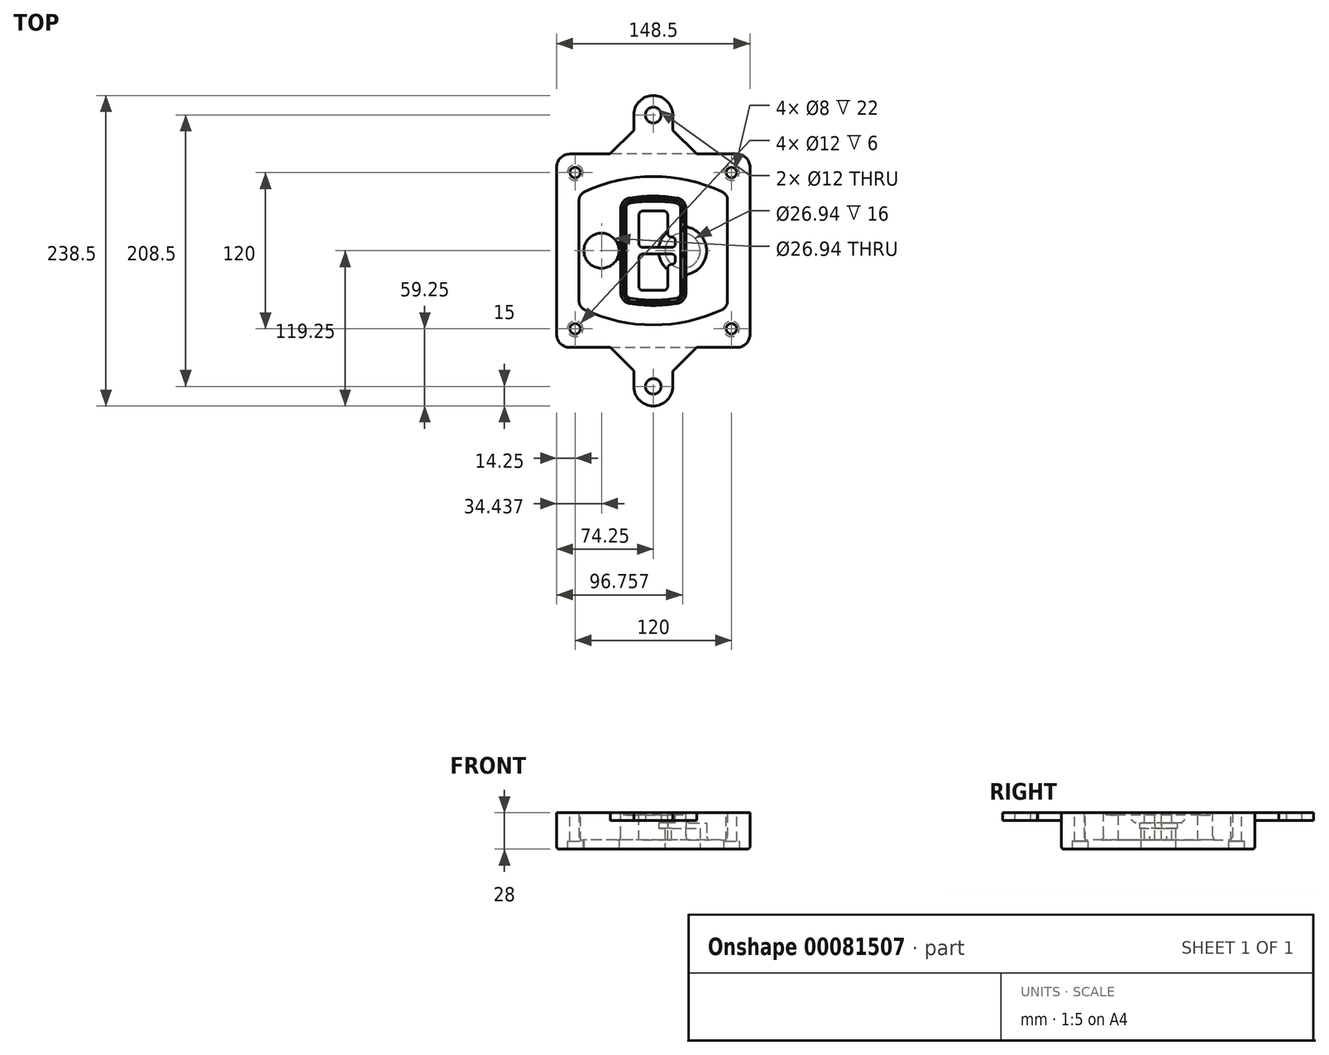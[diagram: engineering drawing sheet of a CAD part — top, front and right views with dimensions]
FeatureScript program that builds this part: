
annotation { "Feature Type Name" : "Feature", "Feature Type Description" : "" }
export const myFeature = defineFeature(function(context is Context, id is Id, definition is map)
    precondition{}
    {
        {
            var Q0;
            Q0=qCreatedBy(makeId("Top.planeOp"),FACE);
            var sketch = newSketch(context, id + "F0", { "sketchPlane" : qUnion([Q0])});
            skPoint(sketch, "E0.rect.middle", {"position": v(0, 0) * mm});
            skLineSegment(sketch, "E1.bottom", {"start": v(-64.25, -74.25) * mm, "end": v(64.25, -74.25) * mm});
            skLineSegment(sketch, "E1.top", {"start": v(-64.25, 74.25) * mm, "end": v(64.25, 74.25) * mm});
            skLineSegment(sketch, "E1.left", {"start": v(-74.25, -64.25) * mm, "end": v(-74.25, 64.25) * mm});
            skLineSegment(sketch, "E1.right", {"start": v(74.25, -64.25) * mm, "end": v(74.25, 64.25) * mm});
            skLineSegment(sketch, "E2", {"start": v(-74.25, 74.25) * mm, "end": v(74.25, -74.25) * mm, "construction": true});
            skLineSegment(sketch, "E3", {"start": v(74.25, 74.25) * mm, "end": v(-74.25, -74.25) * mm, "construction": true});
            skCircle(sketch, "E4", {"center": v(-60, 60) * mm, "radius": 4 * mm});
            skCircle(sketch, "E5", {"center": v(60, 60) * mm, "radius": 4 * mm});
            skCircle(sketch, "E6", {"center": v(60, -60) * mm, "radius": 4 * mm});
            skCircle(sketch, "E7", {"center": v(-60, -60) * mm, "radius": 4 * mm});
            skLineSegment(sketch, "E8", {"start": v(-60, 60) * mm, "end": v(60, 60) * mm, "construction": true});
            skLineSegment(sketch, "E9", {"start": v(60, 60) * mm, "end": v(60, -60) * mm, "construction": true});
            skLineSegment(sketch, "E10", {"start": v(60, -60) * mm, "end": v(-60, -60) * mm, "construction": true});
            skLineSegment(sketch, "E11", {"start": v(-60, -60) * mm, "end": v(-60, 60) * mm, "construction": true});
            skLineSegment(sketch, "E12", {"start": v(-60, 38.83) * mm, "end": v(-60, -38.83) * mm});
            skLineSegment(sketch, "E13", {"start": v(60, 38.83) * mm, "end": v(60, -38.83) * mm});
            skArc(sketch, "E14", {"start": v(54.26, 47.88) * mm, "mid": v(0, 60) * mm, "end": v(-54.26, 47.88) * mm});
            skArc(sketch, "E15", {"start": v(-54.26, -47.88) * mm, "mid": v(0, -60) * mm, "end": v(54.26, -47.88) * mm});
            skLineSegment(sketch, "E16", {"start": v(-60, 0) * mm, "end": v(60, 0) * mm, "construction": true});
            skPoint(sketch, "E17.visualSharp", {"position": v(-60, -45) * mm});
            skArc(sketch, "E17.filletArc", {"start": v(-60, -38.83) * mm, "mid": v(-58.44, -44.2) * mm, "end": v(-54.26, -47.88) * mm});
            skPoint(sketch, "E18.visualSharp", {"position": v(-60, 45) * mm});
            skArc(sketch, "E18.filletArc", {"start": v(-54.26, 47.88) * mm, "mid": v(-58.44, 44.2) * mm, "end": v(-60, 38.83) * mm});
            skPoint(sketch, "E19.visualSharp", {"position": v(60, 45) * mm});
            skArc(sketch, "E19.filletArc", {"start": v(60, 38.83) * mm, "mid": v(58.44, 44.2) * mm, "end": v(54.26, 47.88) * mm});
            skPoint(sketch, "E20.visualSharp", {"position": v(60, -45) * mm});
            skArc(sketch, "E20.filletArc", {"start": v(54.26, -47.88) * mm, "mid": v(58.44, -44.2) * mm, "end": v(60, -38.83) * mm});
            skPoint(sketch, "E21.visualSharp", {"position": v(-74.25, 74.25) * mm});
            skArc(sketch, "E21.filletArc", {"start": v(-64.25, 74.25) * mm, "mid": v(-71.32, 71.32) * mm, "end": v(-74.25, 64.25) * mm});
            skPoint(sketch, "E22.visualSharp", {"position": v(74.25, 74.25) * mm});
            skArc(sketch, "E22.filletArc", {"start": v(74.25, 64.25) * mm, "mid": v(71.32, 71.32) * mm, "end": v(64.25, 74.25) * mm});
            skPoint(sketch, "E23.visualSharp", {"position": v(74.25, -74.25) * mm});
            skArc(sketch, "E23.filletArc", {"start": v(64.25, -74.25) * mm, "mid": v(71.32, -71.32) * mm, "end": v(74.25, -64.25) * mm});
            skPoint(sketch, "E24.visualSharp", {"position": v(-74.25, -74.25) * mm});
            skArc(sketch, "E24.filletArc", {"start": v(-74.25, -64.25) * mm, "mid": v(-71.32, -71.32) * mm, "end": v(-64.25, -74.25) * mm});
            skArc(sketch, "E25.0", {"start": v(57, 38.83) * mm, "mid": v(55.9, 42.58) * mm, "end": v(52.98, 45.17) * mm});
            skLineSegment(sketch, "E25.1", {"start": v(57, 38.83) * mm, "end": v(57, -38.83) * mm});
            skArc(sketch, "E25.2", {"start": v(52.98, -45.17) * mm, "mid": v(55.9, -42.58) * mm, "end": v(57, -38.83) * mm});
            skArc(sketch, "E25.3", {"start": v(-52.98, -45.17) * mm, "mid": v(0, -57) * mm, "end": v(52.98, -45.17) * mm});
            skArc(sketch, "E25.4", {"start": v(-57, -38.83) * mm, "mid": v(-55.9, -42.58) * mm, "end": v(-52.98, -45.17) * mm});
            skArc(sketch, "E25.5", {"start": v(52.98, 45.17) * mm, "mid": v(0, 57) * mm, "end": v(-52.98, 45.17) * mm});
            skLineSegment(sketch, "E25.6", {"start": v(-57, 38.83) * mm, "end": v(-57, -38.83) * mm});
            skArc(sketch, "E25.7", {"start": v(-52.98, 45.17) * mm, "mid": v(-55.9, 42.58) * mm, "end": v(-57, 38.83) * mm});
            skArc(sketch, "E26.0", {"start": v(-55.96, 51.5) * mm, "mid": v(-61.82, 46.33) * mm, "end": v(-64, 38.83) * mm});
            skArc(sketch, "E26.1", {"start": v(55.96, 51.5) * mm, "mid": v(0, 64) * mm, "end": v(-55.96, 51.5) * mm});
            skArc(sketch, "E26.2", {"start": v(64, 38.83) * mm, "mid": v(61.82, 46.33) * mm, "end": v(55.96, 51.5) * mm});
            skLineSegment(sketch, "E26.3", {"start": v(64, 38.83) * mm, "end": v(64, -38.83) * mm});
            skArc(sketch, "E26.4", {"start": v(55.96, -51.5) * mm, "mid": v(61.82, -46.33) * mm, "end": v(64, -38.83) * mm});
            skLineSegment(sketch, "E26.5", {"start": v(-64, 38.83) * mm, "end": v(-64, -38.83) * mm});
            skArc(sketch, "E26.6", {"start": v(-55.96, -51.5) * mm, "mid": v(0, -64) * mm, "end": v(55.96, -51.5) * mm});
            skArc(sketch, "E26.7", {"start": v(-64, -38.83) * mm, "mid": v(-61.82, -46.33) * mm, "end": v(-55.96, -51.5) * mm});
            skSolve(sketch);
        }
        {
            var Q0;
            Q0=makeQuery(id+"F0.imprint","IMPRINT",FACE,{"disambiguationData":[TD([[makeQuery(id+"F0.imprint","IMPRINT",EDGE,{"derivedFrom":sQuery(id+"F0.wireOp",EDGE,"E1.bottom")}),1.0]])]});
            var Q1;
            Q1=makeQuery(id+"F0.imprint","IMPRINT",FACE,{"disambiguationData":[TD([[makeQuery(id+"F0.imprint","IMPRINT",EDGE,{"derivedFrom":sQuery(id+"F0.wireOp",EDGE,"E12")}),1.0]])]});
            var Q2;
            Q2=makeQuery(id+"F0.imprint","IMPRINT",FACE,{"disambiguationData":[TD([[makeQuery(id+"F0.imprint","IMPRINT",EDGE,{"derivedFrom":sQuery(id+"F0.wireOp",EDGE,"E25.0")}),1.0]])]});
            var Q3;
            Q3=makeQuery(id+"F0.imprint","IMPRINT",FACE,{"disambiguationData":[TD([[makeQuery(id+"F0.imprint","IMPRINT",EDGE,{"derivedFrom":sQuery(id+"F0.wireOp",EDGE,"E12")}),-1.0]])]});
            extrude(context, id + "F1", {"entities" : qUnion([Q0, Q1, Q2, Q3]), "oppositeDirection" : true, "depth" : 25 * mm});
        }
        {
            var Q0;
            Q0=makeQuery(id+"F0.imprint","IMPRINT",FACE,{"disambiguationData":[TD([[makeQuery(id+"F0.imprint","IMPRINT",EDGE,{"derivedFrom":sQuery(id+"F0.wireOp",EDGE,"E12")}),1.0]])]});
            extrude(context, id + "F2", {"entities" : qUnion([Q0]), "operationType" : NewBodyOperationType.ADD, "depth" : 3 * mm});
        }
        {
            var Q0;
            Q0=makeQuery(id+"F0.imprint","IMPRINT",FACE,{"disambiguationData":[TD([[makeQuery(id+"F0.imprint","IMPRINT",EDGE,{"derivedFrom":sQuery(id+"F0.wireOp",EDGE,"E25.0")}),1.0]])]});
            extrude(context, id + "F3", {"entities" : qUnion([Q0]), "operationType" : NewBodyOperationType.REMOVE, "oppositeDirection" : true, "depth" : 18 * mm});
        }
        {
            var Q0;
            Q0=makeQuery(id+"F2.opExtrude","CAP_FACE",FACE,{"disambiguationData":[OSD([sQuery(id+"F0.wireOp",EDGE,"E12"),sQuery(id+"F0.wireOp",EDGE,"E13"),sQuery(id+"F0.wireOp",EDGE,"E14"),sQuery(id+"F0.wireOp",EDGE,"E15"),sQuery(id+"F0.wireOp",EDGE,"E17.filletArc"),sQuery(id+"F0.wireOp",EDGE,"E18.filletArc"),sQuery(id+"F0.wireOp",EDGE,"E19.filletArc"),sQuery(id+"F0.wireOp",EDGE,"E20.filletArc"),sQuery(id+"F0.wireOp",EDGE,"E25.0"),sQuery(id+"F0.wireOp",EDGE,"E25.1"),sQuery(id+"F0.wireOp",EDGE,"E25.2"),sQuery(id+"F0.wireOp",EDGE,"E25.3"),sQuery(id+"F0.wireOp",EDGE,"E25.4"),sQuery(id+"F0.wireOp",EDGE,"E25.5"),sQuery(id+"F0.wireOp",EDGE,"E25.6"),sQuery(id+"F0.wireOp",EDGE,"E25.7")])],"isStart":false});
            var sketch = newSketch(context, id + "F4", { "sketchPlane" : qUnion([Q0])});
            skArc(sketch, "E27.0", {"start": v(-18.34, -40.45) * mm, "mid": v(0, -42) * mm, "end": v(18.34, -40.45) * mm});
            skArc(sketch, "E28.0", {"start": v(18.34, 40.45) * mm, "mid": v(0, 42) * mm, "end": v(-18.34, 40.45) * mm});
            skLineSegment(sketch, "E29", {"start": v(-25, 32.57) * mm, "end": v(-25, -32.57) * mm});
            skLineSegment(sketch, "E30", {"start": v(25, 32.57) * mm, "end": v(25, -32.57) * mm});
            skLineSegment(sketch, "E31", {"start": v(-25, 39.1) * mm, "end": v(25, 39.1) * mm, "construction": true});
            skLineSegment(sketch, "E32", {"start": v(-25, -39.1) * mm, "end": v(25, -39.1) * mm, "construction": true});
            skPoint(sketch, "E33.visualSharp", {"position": v(-25, 39.1) * mm});
            skArc(sketch, "E33.filletArc", {"start": v(-18.34, 40.45) * mm, "mid": v(-23.11, 37.73) * mm, "end": v(-25, 32.57) * mm});
            skPoint(sketch, "E34.visualSharp", {"position": v(25, 39.1) * mm});
            skArc(sketch, "E34.filletArc", {"start": v(25, 32.57) * mm, "mid": v(23.11, 37.73) * mm, "end": v(18.34, 40.45) * mm});
            skPoint(sketch, "E35.visualSharp", {"position": v(25, -39.1) * mm});
            skArc(sketch, "E35.filletArc", {"start": v(18.34, -40.45) * mm, "mid": v(23.11, -37.73) * mm, "end": v(25, -32.57) * mm});
            skPoint(sketch, "E36.visualSharp", {"position": v(-25, -39.1) * mm});
            skArc(sketch, "E36.filletArc", {"start": v(-25, -32.57) * mm, "mid": v(-23.11, -37.73) * mm, "end": v(-18.34, -40.45) * mm});
            skArc(sketch, "E37.0", {"start": v(52.98, 45.17) * mm, "mid": v(0, 57) * mm, "end": v(-52.98, 45.17) * mm});
            skArc(sketch, "E37.1", {"start": v(-52.98, 45.17) * mm, "mid": v(-55.9, 42.58) * mm, "end": v(-57, 38.83) * mm});
            skLineSegment(sketch, "E37.2", {"start": v(-57, 38.83) * mm, "end": v(-57, -38.83) * mm});
            skArc(sketch, "E37.3", {"start": v(-57, -38.83) * mm, "mid": v(-55.9, -42.58) * mm, "end": v(-52.98, -45.17) * mm});
            skArc(sketch, "E37.4", {"start": v(-52.98, -45.17) * mm, "mid": v(0, -57) * mm, "end": v(52.98, -45.17) * mm});
            skArc(sketch, "E37.5", {"start": v(52.98, -45.17) * mm, "mid": v(55.9, -42.58) * mm, "end": v(57, -38.83) * mm});
            skLineSegment(sketch, "E37.6", {"start": v(57, 38.83) * mm, "end": v(57, -38.83) * mm});
            skArc(sketch, "E37.7", {"start": v(57, 38.83) * mm, "mid": v(55.9, 42.58) * mm, "end": v(52.98, 45.17) * mm});
            skLineSegment(sketch, "E38.0", {"start": v(23, 32.57) * mm, "end": v(23, -32.57) * mm});
            skArc(sketch, "E38.1", {"start": v(18, -38.48) * mm, "mid": v(21.58, -36.44) * mm, "end": v(23, -32.57) * mm});
            skArc(sketch, "E38.2", {"start": v(-18, -38.48) * mm, "mid": v(0, -40) * mm, "end": v(18, -38.48) * mm});
            skArc(sketch, "E38.3", {"start": v(-23, -32.57) * mm, "mid": v(-21.58, -36.44) * mm, "end": v(-18, -38.48) * mm});
            skLineSegment(sketch, "E38.4", {"start": v(-23, 32.57) * mm, "end": v(-23, -32.57) * mm});
            skArc(sketch, "E38.5", {"start": v(23, 32.57) * mm, "mid": v(21.58, 36.44) * mm, "end": v(18, 38.48) * mm});
            skArc(sketch, "E38.6", {"start": v(-18, 38.48) * mm, "mid": v(-21.58, 36.44) * mm, "end": v(-23, 32.57) * mm});
            skArc(sketch, "E38.7", {"start": v(18, 38.48) * mm, "mid": v(0, 40) * mm, "end": v(-18, 38.48) * mm});
            skArc(sketch, "E39.0", {"start": v(21, 32.57) * mm, "mid": v(20.06, 35.15) * mm, "end": v(17.67, 36.5) * mm});
            skLineSegment(sketch, "E39.1", {"start": v(21, 32.57) * mm, "end": v(21, -32.57) * mm});
            skArc(sketch, "E39.2", {"start": v(17.67, -36.5) * mm, "mid": v(20.06, -35.15) * mm, "end": v(21, -32.57) * mm});
            skArc(sketch, "E39.3", {"start": v(-17.67, -36.5) * mm, "mid": v(0, -38) * mm, "end": v(17.67, -36.5) * mm});
            skArc(sketch, "E39.4", {"start": v(-21, -32.57) * mm, "mid": v(-20.06, -35.15) * mm, "end": v(-17.67, -36.5) * mm});
            skArc(sketch, "E39.5", {"start": v(17.67, 36.5) * mm, "mid": v(0, 38) * mm, "end": v(-17.67, 36.5) * mm});
            skLineSegment(sketch, "E39.6", {"start": v(-21, 32.57) * mm, "end": v(-21, -32.57) * mm});
            skArc(sketch, "E39.7", {"start": v(-17.67, 36.5) * mm, "mid": v(-20.06, 35.15) * mm, "end": v(-21, 32.57) * mm});
            skLineSegment(sketch, "E40", {"start": v(-25, 0) * mm, "end": v(25, 0) * mm, "construction": true});
            skLineSegment(sketch, "E41", {"start": v(-11, 5.5) * mm, "end": v(-11, 27.5) * mm});
            skLineSegment(sketch, "E42", {"start": v(-8, 30.5) * mm, "end": v(8, 30.5) * mm});
            skLineSegment(sketch, "E43", {"start": v(11, 27.5) * mm, "end": v(11, 13.5) * mm});
            skLineSegment(sketch, "E44", {"start": v(14, 10.5) * mm, "end": v(14, 10.5) * mm});
            skLineSegment(sketch, "E45", {"start": v(17, 7.5) * mm, "end": v(17, 5.5) * mm});
            skLineSegment(sketch, "E46", {"start": v(14, 2.5) * mm, "end": v(-8, 2.5) * mm});
            skPoint(sketch, "E47.visualSharp", {"position": v(-11, 30.5) * mm});
            skArc(sketch, "E47.filletArc", {"start": v(-8, 30.5) * mm, "mid": v(-10.12, 29.62) * mm, "end": v(-11, 27.5) * mm});
            skPoint(sketch, "E48.visualSharp", {"position": v(11, 30.5) * mm});
            skArc(sketch, "E48.filletArc", {"start": v(11, 27.5) * mm, "mid": v(10.12, 29.62) * mm, "end": v(8, 30.5) * mm});
            skPoint(sketch, "E49.visualSharp", {"position": v(11, 10.5) * mm});
            skArc(sketch, "E49.filletArc", {"start": v(11, 13.5) * mm, "mid": v(11.88, 11.38) * mm, "end": v(14, 10.5) * mm});
            skPoint(sketch, "E50.visualSharp", {"position": v(17, 10.5) * mm});
            skArc(sketch, "E50.filletArc", {"start": v(17, 7.5) * mm, "mid": v(16.12, 9.62) * mm, "end": v(14, 10.5) * mm});
            skPoint(sketch, "E51.visualSharp", {"position": v(17, 2.5) * mm});
            skArc(sketch, "E51.filletArc", {"start": v(14, 2.5) * mm, "mid": v(16.12, 3.38) * mm, "end": v(17, 5.5) * mm});
            skPoint(sketch, "E52.visualSharp", {"position": v(-11, 2.5) * mm});
            skArc(sketch, "E52.filletArc", {"start": v(-11, 5.5) * mm, "mid": v(-10.12, 3.38) * mm, "end": v(-8, 2.5) * mm});
            skLineSegment(sketch, "E53.0.MirrorCS", {"start": v(14, -2.5) * mm, "end": v(-8, -2.5) * mm});
            skArc(sketch, "E54.0.MirrorCS", {"start": v(-11, -5.5) * mm, "mid": v(-10.12, -3.38) * mm, "end": v(-8, -2.5) * mm});
            skLineSegment(sketch, "E55.0.MirrorCS", {"start": v(-11, -5.5) * mm, "end": v(-11, -27.5) * mm});
            skArc(sketch, "E56.0.MirrorCS", {"start": v(-8, -30.5) * mm, "mid": v(-10.12, -29.62) * mm, "end": v(-11, -27.5) * mm});
            skLineSegment(sketch, "E57.0.MirrorCS", {"start": v(-8, -30.5) * mm, "end": v(8, -30.5) * mm});
            skArc(sketch, "E58.0.MirrorCS", {"start": v(11, -27.5) * mm, "mid": v(10.12, -29.62) * mm, "end": v(8, -30.5) * mm});
            skLineSegment(sketch, "E59.0.MirrorCS", {"start": v(11, -27.5) * mm, "end": v(11, -13.5) * mm});
            skArc(sketch, "E60.0.MirrorCS", {"start": v(11, -13.5) * mm, "mid": v(11.88, -11.38) * mm, "end": v(14, -10.5) * mm});
            skArc(sketch, "E61.0.MirrorCS", {"start": v(17, -7.5) * mm, "mid": v(16.12, -9.62) * mm, "end": v(14, -10.5) * mm});
            skLineSegment(sketch, "E62.0.MirrorCS", {"start": v(17, -7.5) * mm, "end": v(17, -5.5) * mm});
            skArc(sketch, "E63.0.MirrorCS", {"start": v(14, -2.5) * mm, "mid": v(16.12, -3.38) * mm, "end": v(17, -5.5) * mm});
            skSolve(sketch);
        }
        {
            var Q0;
            Q0=makeQuery(id+"F4.imprint","IMPRINT",FACE,{"disambiguationData":[TD([[makeQuery(id+"F4.imprint","IMPRINT",EDGE,{"derivedFrom":sQuery(id+"F4.wireOp",EDGE,"E27.0")}),1.0]])]});
            var Q1;
            Q1=makeQuery(id+"F4.imprint","IMPRINT",FACE,{"disambiguationData":[TD([[makeQuery(id+"F4.imprint","IMPRINT",EDGE,{"derivedFrom":sQuery(id+"F4.wireOp",EDGE,"E38.0")}),-1.0]])]});
            var Q2;
            Q2=makeQuery(id+"F4.imprint","IMPRINT",FACE,{"disambiguationData":[TD([[makeQuery(id+"F4.imprint","IMPRINT",EDGE,{"derivedFrom":sQuery(id+"F4.wireOp",EDGE,"E39.0")}),1.0]])]});
            extrude(context, id + "F5", {"entities" : qUnion([Q0, Q1, Q2]), "operationType" : NewBodyOperationType.ADD, "endBound" : BoundingType.UP_TO_NEXT, "oppositeDirection" : true, "depth" : 25 * mm});
        }
        {
            var Q0;
            Q0=makeQuery(id+"F4.imprint","IMPRINT",FACE,{"disambiguationData":[TD([[makeQuery(id+"F4.imprint","IMPRINT",EDGE,{"derivedFrom":sQuery(id+"F4.wireOp",EDGE,"E38.0")}),-1.0]])]});
            extrude(context, id + "F6", {"entities" : qUnion([Q0]), "operationType" : NewBodyOperationType.REMOVE, "oppositeDirection" : true, "depth" : 2 * mm});
        }
        {
            var Q0;
            Q0=makeQuery(id+"F1.opExtrude","CAP_FACE",FACE,{"disambiguationData":[OSD([sQuery(id+"F0.wireOp",EDGE,"E1.bottom"),sQuery(id+"F0.wireOp",EDGE,"E1.top"),sQuery(id+"F0.wireOp",EDGE,"E1.left"),sQuery(id+"F0.wireOp",EDGE,"E1.right"),sQuery(id+"F0.wireOp",EDGE,"E4"),sQuery(id+"F0.wireOp",EDGE,"E5"),sQuery(id+"F0.wireOp",EDGE,"E6"),sQuery(id+"F0.wireOp",EDGE,"E7"),sQuery(id+"F0.wireOp",EDGE,"E21.filletArc"),sQuery(id+"F0.wireOp",EDGE,"E22.filletArc"),sQuery(id+"F0.wireOp",EDGE,"E23.filletArc"),sQuery(id+"F0.wireOp",EDGE,"E24.filletArc")])],"isStart":false});
            var sketch = newSketch(context, id + "F7", { "sketchPlane" : qUnion([Q0])});
            skCircle(sketch, "E64", {"center": v(22.5, 0) * mm, "radius": 13.47 * mm});
            skCircle(sketch, "E65", {"center": v(-39.81, 0) * mm, "radius": 13.47 * mm});
            skLineSegment(sketch, "E66", {"start": v(74.25, 0) * mm, "end": v(-74.25, 0) * mm});
            skCircle(sketch, "E67", {"center": v(22.5, 0) * mm, "radius": 18.47 * mm});
            skCircle(sketch, "E68", {"center": v(60, -60) * mm, "radius": 6 * mm});
            skCircle(sketch, "E69", {"center": v(-60, -60) * mm, "radius": 6 * mm});
            skCircle(sketch, "E70", {"center": v(-60, 60) * mm, "radius": 6 * mm});
            skCircle(sketch, "E71", {"center": v(60, 60) * mm, "radius": 6 * mm});
            skSolve(sketch);
        }
        {
            var Q0;
            {var subQ1=sQuery(id+"F7.wireOp",EDGE,"E66");var subQ4=sQuery(id+"F7.wireOp",EDGE,"E64");var subQ6=makeQuery(id+"F7.imprint","INTERSECT",VERTEX,{"disambiguationData":[OD(0.0)],"derivedFrom":[subQ4,subQ1]});Q0=makeQuery(id+"F7.imprint","IMPRINT",FACE,{"disambiguationData":[TD([[makeQuery(id+"F7.imprint","IMPRINT",EDGE,{"disambiguationData":[TD([[subQ6,-1.0]])],"derivedFrom":subQ4}),-1.0]])]});}
            var Q1;
            {var subQ0=sQuery(id+"F7.wireOp",EDGE,"E66");var subQ1=sQuery(id+"F7.wireOp",EDGE,"E64");var subQ3=makeQuery(id+"F7.imprint","INTERSECT",VERTEX,{"disambiguationData":[OD(0.0)],"derivedFrom":[subQ1,subQ0]});Q1=makeQuery(id+"F7.imprint","IMPRINT",FACE,{"disambiguationData":[TD([[makeQuery(id+"F7.imprint","IMPRINT",EDGE,{"disambiguationData":[TD([[subQ3,-1.0]])],"derivedFrom":subQ1}),1.0]])]});}
            var Q2;
            {var subQ0=sQuery(id+"F7.wireOp",EDGE,"E66");var subQ1=sQuery(id+"F7.wireOp",EDGE,"E64");var subQ3=makeQuery(id+"F7.imprint","INTERSECT",VERTEX,{"disambiguationData":[OD(0.0)],"derivedFrom":[subQ1,subQ0]});Q2=makeQuery(id+"F7.imprint","IMPRINT",FACE,{"disambiguationData":[TD([[makeQuery(id+"F7.imprint","IMPRINT",EDGE,{"disambiguationData":[TD([[subQ3,1.0]])],"derivedFrom":subQ1}),1.0]])]});}
            var Q3;
            {var subQ1=sQuery(id+"F7.wireOp",EDGE,"E66");var subQ4=sQuery(id+"F7.wireOp",EDGE,"E64");var subQ6=makeQuery(id+"F7.imprint","INTERSECT",VERTEX,{"disambiguationData":[OD(0.0)],"derivedFrom":[subQ4,subQ1]});Q3=makeQuery(id+"F7.imprint","IMPRINT",FACE,{"disambiguationData":[TD([[makeQuery(id+"F7.imprint","IMPRINT",EDGE,{"disambiguationData":[TD([[subQ6,1.0]])],"derivedFrom":subQ4}),-1.0]])]});}
            extrude(context, id + "F8", {"entities" : qUnion([Q0, Q1, Q2, Q3]), "operationType" : NewBodyOperationType.ADD, "oppositeDirection" : true, "depth" : 20 * mm});
        }
        {
            var Q0;
            {var subQ0=sQuery(id+"F7.wireOp",EDGE,"E66");var subQ1=sQuery(id+"F7.wireOp",EDGE,"E64");var subQ3=makeQuery(id+"F7.imprint","INTERSECT",VERTEX,{"disambiguationData":[OD(0.0)],"derivedFrom":[subQ1,subQ0]});Q0=makeQuery(id+"F7.imprint","IMPRINT",FACE,{"disambiguationData":[TD([[makeQuery(id+"F7.imprint","IMPRINT",EDGE,{"disambiguationData":[TD([[subQ3,-1.0]])],"derivedFrom":subQ1}),1.0]])]});}
            var Q1;
            {var subQ0=sQuery(id+"F7.wireOp",EDGE,"E66");var subQ1=sQuery(id+"F7.wireOp",EDGE,"E64");var subQ3=makeQuery(id+"F7.imprint","INTERSECT",VERTEX,{"disambiguationData":[OD(0.0)],"derivedFrom":[subQ1,subQ0]});Q1=makeQuery(id+"F7.imprint","IMPRINT",FACE,{"disambiguationData":[TD([[makeQuery(id+"F7.imprint","IMPRINT",EDGE,{"disambiguationData":[TD([[subQ3,1.0]])],"derivedFrom":subQ1}),1.0]])]});}
            extrude(context, id + "F9", {"entities" : qUnion([Q0, Q1]), "operationType" : NewBodyOperationType.REMOVE, "oppositeDirection" : true, "depth" : 16 * mm});
        }
        {
            var Q0;
            {var subQ0=sQuery(id+"F7.wireOp",EDGE,"E66");var subQ1=sQuery(id+"F7.wireOp",EDGE,"E65");var subQ3=makeQuery(id+"F7.imprint","INTERSECT",VERTEX,{"disambiguationData":[OD(0.0)],"derivedFrom":[subQ1,subQ0]});Q0=makeQuery(id+"F7.imprint","IMPRINT",FACE,{"disambiguationData":[TD([[makeQuery(id+"F7.imprint","IMPRINT",EDGE,{"disambiguationData":[TD([[subQ3,-1.0]])],"derivedFrom":subQ1}),1.0]])]});}
            var Q1;
            {var subQ0=sQuery(id+"F7.wireOp",EDGE,"E66");var subQ1=sQuery(id+"F7.wireOp",EDGE,"E65");var subQ3=makeQuery(id+"F7.imprint","INTERSECT",VERTEX,{"disambiguationData":[OD(0.0)],"derivedFrom":[subQ1,subQ0]});Q1=makeQuery(id+"F7.imprint","IMPRINT",FACE,{"disambiguationData":[TD([[makeQuery(id+"F7.imprint","IMPRINT",EDGE,{"disambiguationData":[TD([[subQ3,1.0]])],"derivedFrom":subQ1}),1.0]])]});}
            extrude(context, id + "F10", {"entities" : qUnion([Q0, Q1]), "operationType" : NewBodyOperationType.REMOVE, "oppositeDirection" : true, "depth" : 25 * mm});
        }
        {
            var Q0;
            Q0=makeQuery(id+"F7.imprint","IMPRINT",FACE,{"disambiguationData":[TD([[makeQuery(id+"F7.imprint","IMPRINT",EDGE,{"derivedFrom":sQuery(id+"F7.wireOp",EDGE,"E68")}),1.0]])]});
            var Q1;
            Q1=makeQuery(id+"F7.imprint","IMPRINT",FACE,{"disambiguationData":[TD([[makeQuery(id+"F7.imprint","IMPRINT",EDGE,{"derivedFrom":makeQuery(id+"F1.opExtrude","CAP_EDGE",EDGE,{"disambiguationData":[OSD([sQuery(id+"F0.wireOp",EDGE,"E5")])],"isStart":false})}),-1.0]])]});
            var Q2;
            Q2=makeQuery(id+"F7.imprint","IMPRINT",FACE,{"disambiguationData":[TD([[makeQuery(id+"F7.imprint","IMPRINT",EDGE,{"derivedFrom":sQuery(id+"F7.wireOp",EDGE,"E69")}),1.0]])]});
            var Q3;
            Q3=makeQuery(id+"F7.imprint","IMPRINT",FACE,{"disambiguationData":[TD([[makeQuery(id+"F7.imprint","IMPRINT",EDGE,{"derivedFrom":makeQuery(id+"F1.opExtrude","CAP_EDGE",EDGE,{"disambiguationData":[OSD([sQuery(id+"F0.wireOp",EDGE,"E4")])],"isStart":false})}),-1.0]])]});
            var Q4;
            Q4=makeQuery(id+"F7.imprint","IMPRINT",FACE,{"disambiguationData":[TD([[makeQuery(id+"F7.imprint","IMPRINT",EDGE,{"derivedFrom":sQuery(id+"F7.wireOp",EDGE,"E70")}),1.0]])]});
            var Q5;
            Q5=makeQuery(id+"F7.imprint","IMPRINT",FACE,{"disambiguationData":[TD([[makeQuery(id+"F7.imprint","IMPRINT",EDGE,{"derivedFrom":makeQuery(id+"F1.opExtrude","CAP_EDGE",EDGE,{"disambiguationData":[OSD([sQuery(id+"F0.wireOp",EDGE,"E7")])],"isStart":false})}),-1.0]])]});
            var Q6;
            Q6=makeQuery(id+"F7.imprint","IMPRINT",FACE,{"disambiguationData":[TD([[makeQuery(id+"F7.imprint","IMPRINT",EDGE,{"derivedFrom":sQuery(id+"F7.wireOp",EDGE,"E71")}),1.0]])]});
            var Q7;
            Q7=makeQuery(id+"F7.imprint","IMPRINT",FACE,{"disambiguationData":[TD([[makeQuery(id+"F7.imprint","IMPRINT",EDGE,{"derivedFrom":makeQuery(id+"F1.opExtrude","CAP_EDGE",EDGE,{"disambiguationData":[OSD([sQuery(id+"F0.wireOp",EDGE,"E6")])],"isStart":false})}),-1.0]])]});
            extrude(context, id + "F11", {"entities" : qUnion([Q0, Q1, Q2, Q3, Q4, Q5, Q6, Q7]), "operationType" : NewBodyOperationType.REMOVE, "oppositeDirection" : true, "depth" : 6 * mm});
        }
        {
            var Q0;
            Q0=makeQuery(id+"F9.boolean.opBoolean","COPY",FACE,{"derivedFrom":makeQuery(id+"F9.opExtrude","CAP_FACE",FACE,{"disambiguationData":[OSD([sQuery(id+"F7.wireOp",EDGE,"E64")])],"isStart":false})});
            var sketch = newSketch(context, id + "F12", { "sketchPlane" : qUnion([Q0])});
            skArc(sketch, "E72.0", {"start": v(11, 14.45) * mm, "mid": v(6.45, 9.13) * mm, "end": v(4.2, 2.5) * mm});
            skArc(sketch, "E72.1", {"start": v(4.2, -2.5) * mm, "mid": v(6.45, -9.13) * mm, "end": v(11, -14.45) * mm});
            skLineSegment(sketch, "E73", {"start": v(4.2, -2.5) * mm, "end": v(14, -2.5) * mm});
            skLineSegment(sketch, "E74.0", {"start": v(14, 2.5) * mm, "end": v(4.2, 2.5) * mm});
            skArc(sketch, "E74.1", {"start": v(14, 2.5) * mm, "mid": v(16.12, 3.38) * mm, "end": v(17, 5.5) * mm});
            skLineSegment(sketch, "E74.2", {"start": v(17, 7.5) * mm, "end": v(17, 5.5) * mm});
            skArc(sketch, "E74.3", {"start": v(17, 7.5) * mm, "mid": v(16.12, 9.62) * mm, "end": v(14, 10.5) * mm});
            skArc(sketch, "E74.4", {"start": v(11, 13.5) * mm, "mid": v(11.88, 11.38) * mm, "end": v(14, 10.5) * mm});
            skLineSegment(sketch, "E74.5", {"start": v(11, 14.45) * mm, "end": v(11, 13.5) * mm});
            skLineSegment(sketch, "E74.7", {"start": v(14, -2.5) * mm, "end": v(4.2, -2.5) * mm});
            skArc(sketch, "E74.8", {"start": v(14, -2.5) * mm, "mid": v(16.12, -3.38) * mm, "end": v(17, -5.5) * mm});
            skLineSegment(sketch, "E74.9", {"start": v(17, -7.5) * mm, "end": v(17, -5.5) * mm});
            skArc(sketch, "E74.10", {"start": v(17, -7.5) * mm, "mid": v(16.12, -9.62) * mm, "end": v(14, -10.5) * mm});
            skArc(sketch, "E74.11", {"start": v(11, -13.5) * mm, "mid": v(11.88, -11.38) * mm, "end": v(14, -10.5) * mm});
            skLineSegment(sketch, "E74.12", {"start": v(11, -14.45) * mm, "end": v(11, -13.5) * mm});
            skPoint(sketch, "E75.orphan", {"position": v(11, -27.5) * mm});
            skPoint(sketch, "E76.orphan", {"position": v(-8, -2.5) * mm});
            skPoint(sketch, "E77.orphan", {"position": v(-8, 2.5) * mm});
            skPoint(sketch, "E78.orphan", {"position": v(11, 27.5) * mm});
            skSolve(sketch);
        }
        {
            var Q0;
            {var subQ7=sQuery(id+"F12.wireOp",EDGE,"E72.0");var subQ14=sQuery(id+"F12.wireOp",EDGE,"E72.1");var subQ16=sQuery(id+"F12.wireOp",EDGE,"E74.1");var subQ18=sQuery(id+"F12.wireOp",EDGE,"E74.8");Q0=qUnion([makeQuery(id+"F12.imprint","IMPRINT",FACE,{"disambiguationData":[TD([[makeQuery(id+"F12.imprint","IMPRINT",EDGE,{"derivedFrom":subQ7}),1.0]])]}),makeQuery(id+"F12.imprint","IMPRINT",FACE,{"disambiguationData":[TD([[makeQuery(id+"F12.imprint","IMPRINT",EDGE,{"derivedFrom":subQ14}),1.0]])]}),makeQuery(id+"F12.imprint","IMPRINT",FACE,{"disambiguationData":[TD([[makeQuery(id+"F12.imprint","IMPRINT",EDGE,{"derivedFrom":subQ16}),1.0]])]}),makeQuery(id+"F12.imprint","IMPRINT",FACE,{"disambiguationData":[TD([[makeQuery(id+"F12.imprint","IMPRINT",EDGE,{"derivedFrom":subQ18}),-1.0]])]})]);}
            var Q1;
            Q1=makeQuery(id+"F5.boolean.opBoolean","SPLIT",FACE,{"disambiguationData":[TD([makeQuery(id+"F5.opExtrude","SWEPT_FACE",FACE,{"disambiguationData":[OSD([sQuery(id+"F4.wireOp",EDGE,"E41")])]})])],"derivedFrom":makeQuery(id+"F3.boolean.opBoolean","COPY",FACE,{"derivedFrom":makeQuery(id+"F3.opExtrude","CAP_FACE",FACE,{"disambiguationData":[OSD([sQuery(id+"F0.wireOp",EDGE,"E25.0"),sQuery(id+"F0.wireOp",EDGE,"E25.1"),sQuery(id+"F0.wireOp",EDGE,"E25.2"),sQuery(id+"F0.wireOp",EDGE,"E25.3"),sQuery(id+"F0.wireOp",EDGE,"E25.4"),sQuery(id+"F0.wireOp",EDGE,"E25.5"),sQuery(id+"F0.wireOp",EDGE,"E25.6"),sQuery(id+"F0.wireOp",EDGE,"E25.7")])],"isStart":false})})});
            extrude(context, id + "F13", {"entities" : qUnion([Q0]), "operationType" : NewBodyOperationType.REMOVE, "endBound" : BoundingType.UP_TO_SURFACE, "endBoundEntityFace" : qUnion([Q1]), "depth" : 25 * mm});
        }
        {
            var Q0;
            Q0=makeQuery(id+"F3.boolean.opBoolean","COPY",EDGE,{"derivedFrom":makeQuery(id+"F3.opExtrude","CAP_EDGE",EDGE,{"disambiguationData":[OSD([sQuery(id+"F0.wireOp",EDGE,"E25.6")])],"isStart":false})});
            var Q1;
            Q1=makeQuery(id+"F8.boolean.opBoolean","INTERSECT",EDGE,{"derivedFrom":[makeQuery(id+"F5.opExtrude","SWEPT_FACE",FACE,{"disambiguationData":[OSD([sQuery(id+"F4.wireOp",EDGE,"E30")])]}),makeQuery(id+"F8.opExtrude","CAP_FACE",FACE,{"disambiguationData":[OSD([sQuery(id+"F7.wireOp",EDGE,"E67")])],"isStart":false})]});
            var Q2;
            Q2=makeQuery(id+"F8.boolean.opBoolean","INTERSECT",EDGE,{"disambiguationData":[OD(1.0)],"derivedFrom":[makeQuery(id+"F5.opExtrude","SWEPT_FACE",FACE,{"disambiguationData":[OSD([sQuery(id+"F4.wireOp",EDGE,"E30")])]}),makeQuery(id+"F8.opExtrude","SWEPT_FACE",FACE,{"disambiguationData":[OSD([sQuery(id+"F7.wireOp",EDGE,"E67")])]})]});
            var Q3;
            {var subQ0=sQuery(id+"F4.wireOp",EDGE,"E30");Q3=makeQuery(id+"F8.boolean.opBoolean","SPLIT",EDGE,{"disambiguationData":[TD([makeQuery(id+"F5.opExtrude","SWEPT_FACE",FACE,{"disambiguationData":[OSD([sQuery(id+"F4.wireOp",EDGE,"E35.filletArc")])]})])],"derivedFrom":makeQuery(id+"F5.opExtrude","CAP_EDGE",EDGE,{"disambiguationData":[OSD([subQ0])],"isStart":false})});}
            var Q4;
            {var subQ0=sQuery(id+"F0.wireOp",EDGE,"E25.7");var subQ1=sQuery(id+"F0.wireOp",EDGE,"E25.1");var subQ2=sQuery(id+"F0.wireOp",EDGE,"E25.6");var subQ3=sQuery(id+"F0.wireOp",EDGE,"E25.5");var subQ4=sQuery(id+"F0.wireOp",EDGE,"E25.4");var subQ5=sQuery(id+"F0.wireOp",EDGE,"E25.0");var subQ6=sQuery(id+"F0.wireOp",EDGE,"E25.2");var subQ7=sQuery(id+"F0.wireOp",EDGE,"E25.3");Q4=makeQuery(id+"F8.boolean.opBoolean","INTERSECT",EDGE,{"derivedFrom":[makeQuery(id+"F5.boolean.opBoolean","SPLIT",FACE,{"disambiguationData":[TD([makeQuery(id+"F2.opExtrude","SWEPT_FACE",FACE,{"disambiguationData":[OSD([subQ5])]})])],"derivedFrom":makeQuery(id+"F3.boolean.opBoolean","COPY",FACE,{"derivedFrom":makeQuery(id+"F3.opExtrude","CAP_FACE",FACE,{"disambiguationData":[OSD([subQ5,subQ1,subQ6,subQ7,subQ4,subQ3,subQ2,subQ0])],"isStart":false})})}),makeQuery(id+"F8.opExtrude","SWEPT_FACE",FACE,{"disambiguationData":[OSD([sQuery(id+"F7.wireOp",EDGE,"E67")])]})]});}
            var Q5;
            Q5=makeQuery(id+"F8.boolean.opBoolean","INTERSECT",EDGE,{"disambiguationData":[OD(0.0)],"derivedFrom":[makeQuery(id+"F5.opExtrude","SWEPT_FACE",FACE,{"disambiguationData":[OSD([sQuery(id+"F4.wireOp",EDGE,"E30")])]}),makeQuery(id+"F8.opExtrude","SWEPT_FACE",FACE,{"disambiguationData":[OSD([sQuery(id+"F7.wireOp",EDGE,"E67")])]})]});
            fillet(context, id + "F14", {"entities" : qUnion([Q0, Q1, Q2, Q3, Q4, Q5]), "radius" : 3 * mm, "tangentPropagation" : true, "allowEdgeOverflow" : false});
        }
        {
            var Q0;
            Q0=makeQuery(id+"F1.opExtrude","CAP_EDGE",EDGE,{"disambiguationData":[OSD([sQuery(id+"F0.wireOp",EDGE,"E1.bottom")])],"isStart":false});
            fillet(context, id + "F15", {"entities" : qUnion([Q0]), "radius" : 2 * mm, "tangentPropagation" : true, "allowEdgeOverflow" : false});
        }
        {
            var Q0;
            {var subQ0=sQuery(id+"F0.wireOp",EDGE,"E22.filletArc");var subQ1=sQuery(id+"F0.wireOp",EDGE,"E7");var subQ2=sQuery(id+"F0.wireOp",EDGE,"E6");var subQ3=sQuery(id+"F0.wireOp",EDGE,"E5");var subQ4=sQuery(id+"F0.wireOp",EDGE,"E4");var subQ5=sQuery(id+"F0.wireOp",EDGE,"E1.bottom");var subQ6=sQuery(id+"F0.wireOp",EDGE,"E21.filletArc");var subQ7=sQuery(id+"F0.wireOp",EDGE,"E1.top");var subQ8=sQuery(id+"F0.wireOp",EDGE,"E1.left");var subQ9=sQuery(id+"F0.wireOp",EDGE,"E1.right");var subQ10=sQuery(id+"F0.wireOp",EDGE,"E23.filletArc");var subQ11=sQuery(id+"F0.wireOp",EDGE,"E24.filletArc");Q0=makeQuery(id+"F2.boolean.opBoolean","SPLIT",FACE,{"disambiguationData":[TD([makeQuery(id+"F1.opExtrude","SWEPT_FACE",FACE,{"disambiguationData":[OSD([subQ5])]})])],"derivedFrom":makeQuery(id+"F1.opExtrude","CAP_FACE",FACE,{"disambiguationData":[OSD([subQ5,subQ7,subQ8,subQ9,subQ4,subQ3,subQ2,subQ1,subQ6,subQ0,subQ10,subQ11])],"isStart":true})});}
            var sketch = newSketch(context, id + "F16", { "sketchPlane" : qUnion([Q0])});
            skLineSegment(sketch, "E79.0", {"start": v(-64.25, 74.25) * mm, "end": v(64.25, 74.25) * mm});
            skArc(sketch, "E79.1", {"start": v(-64.25, 74.25) * mm, "mid": v(-71.32, 71.32) * mm, "end": v(-74.25, 64.25) * mm});
            skLineSegment(sketch, "E79.2", {"start": v(-74.25, -64.25) * mm, "end": v(-74.25, 64.25) * mm});
            skArc(sketch, "E79.3", {"start": v(-74.25, -64.25) * mm, "mid": v(-71.32, -71.32) * mm, "end": v(-64.25, -74.25) * mm});
            skLineSegment(sketch, "E79.4", {"start": v(-64.25, -74.25) * mm, "end": v(64.25, -74.25) * mm});
            skArc(sketch, "E79.5", {"start": v(64.25, -74.25) * mm, "mid": v(71.32, -71.32) * mm, "end": v(74.25, -64.25) * mm});
            skLineSegment(sketch, "E79.6", {"start": v(74.25, -64.25) * mm, "end": v(74.25, 64.25) * mm});
            skArc(sketch, "E79.7", {"start": v(74.25, 64.25) * mm, "mid": v(71.32, 71.32) * mm, "end": v(64.25, 74.25) * mm});
            skCircle(sketch, "E79.8", {"center": v(60, 60) * mm, "radius": 4 * mm});
            skCircle(sketch, "E79.9", {"center": v(60, -60) * mm, "radius": 4 * mm});
            skCircle(sketch, "E79.10", {"center": v(-60, -60) * mm, "radius": 4 * mm});
            skCircle(sketch, "E79.11", {"center": v(-60, 60) * mm, "radius": 4 * mm});
            skLineSegment(sketch, "E79.12", {"start": v(-60, 38.83) * mm, "end": v(-60, -38.83) * mm});
            skArc(sketch, "E79.13", {"start": v(-54.26, 47.88) * mm, "mid": v(-58.44, 44.2) * mm, "end": v(-60, 38.83) * mm});
            skArc(sketch, "E79.14", {"start": v(54.26, 47.88) * mm, "mid": v(0, 60) * mm, "end": v(-54.26, 47.88) * mm});
            skArc(sketch, "E79.15", {"start": v(60, 38.83) * mm, "mid": v(58.44, 44.2) * mm, "end": v(54.26, 47.88) * mm});
            skLineSegment(sketch, "E79.16", {"start": v(60, 38.83) * mm, "end": v(60, -38.83) * mm});
            skArc(sketch, "E79.17", {"start": v(54.26, -47.88) * mm, "mid": v(58.44, -44.2) * mm, "end": v(60, -38.83) * mm});
            skArc(sketch, "E79.18", {"start": v(-54.26, -47.88) * mm, "mid": v(0, -60) * mm, "end": v(54.26, -47.88) * mm});
            skArc(sketch, "E79.19", {"start": v(-60, -38.83) * mm, "mid": v(-58.44, -44.2) * mm, "end": v(-54.26, -47.88) * mm});
            skLineSegment(sketch, "E80", {"start": v(0, 74.25) * mm, "end": v(0, 104.25) * mm, "construction": true});
            skCircle(sketch, "E81", {"center": v(0, 104.25) * mm, "radius": 6 * mm});
            skLineSegment(sketch, "E82", {"start": v(33.3, 74.25) * mm, "end": v(15, 92.56) * mm});
            skLineSegment(sketch, "E83", {"start": v(15, 92.56) * mm, "end": v(15, 104.25) * mm});
            skLineSegment(sketch, "E84", {"start": v(-33, 74.25) * mm, "end": v(-15, 92.25) * mm});
            skLineSegment(sketch, "E85", {"start": v(-15, 92.25) * mm, "end": v(-15, 104.25) * mm});
            skArc(sketch, "E86", {"start": v(15, 104.25) * mm, "mid": v(0, 119.25) * mm, "end": v(-15, 104.25) * mm});
            skLineSegment(sketch, "E87.MirrorCS", {"start": v(15, 92.25) * mm, "end": v(15, 104.25) * mm});
            skLineSegment(sketch, "E88.MirrorCS", {"start": v(-15, 92.56) * mm, "end": v(-15, 104.25) * mm});
            skLineSegment(sketch, "E89.MirrorCS", {"start": v(-33.3, 74.25) * mm, "end": v(-15, 92.56) * mm});
            skLineSegment(sketch, "E90.MirrorCS", {"start": v(33, 74.25) * mm, "end": v(15, 92.25) * mm});
            skArc(sketch, "E91.MirrorCS", {"start": v(-15, 104.25) * mm, "mid": v(0, 119.25) * mm, "end": v(15, 104.25) * mm});
            skLineSegment(sketch, "E92.MirrorCS", {"start": v(64.25, 74.25) * mm, "end": v(-64.25, 74.25) * mm});
            skLineSegment(sketch, "E93", {"start": v(-74.25, 0) * mm, "end": v(74.25, 0) * mm, "construction": true});
            skArc(sketch, "E94.MirrorCS", {"start": v(15, -104.25) * mm, "mid": v(0, -119.25) * mm, "end": v(-15, -104.25) * mm});
            skLineSegment(sketch, "E95.MirrorCS", {"start": v(15, -92.56) * mm, "end": v(15, -104.25) * mm});
            skLineSegment(sketch, "E96.MirrorCS", {"start": v(-15, -92.25) * mm, "end": v(-15, -104.25) * mm});
            skLineSegment(sketch, "E97.MirrorCS", {"start": v(-33, -74.25) * mm, "end": v(-15, -92.25) * mm});
            skLineSegment(sketch, "E98.MirrorCS", {"start": v(33.3, -74.25) * mm, "end": v(15, -92.56) * mm});
            skLineSegment(sketch, "E99.MirrorCS", {"start": v(0, -74.25) * mm, "end": v(0, -104.25) * mm, "construction": true});
            skCircle(sketch, "E100.MirrorC", {"center": v(0, -104.25) * mm, "radius": 6 * mm});
            skSolve(sketch);
        }
        {
            var Q0;
            Q0 = qSketchRegion(id + "F16", true);
            extrude(context, id + "F17", {"entities" : qUnion([Q0]), "operationType" : NewBodyOperationType.ADD, "endBound" : BoundingType.SYMMETRIC, "depth" : 6 * mm});
        }
    });
